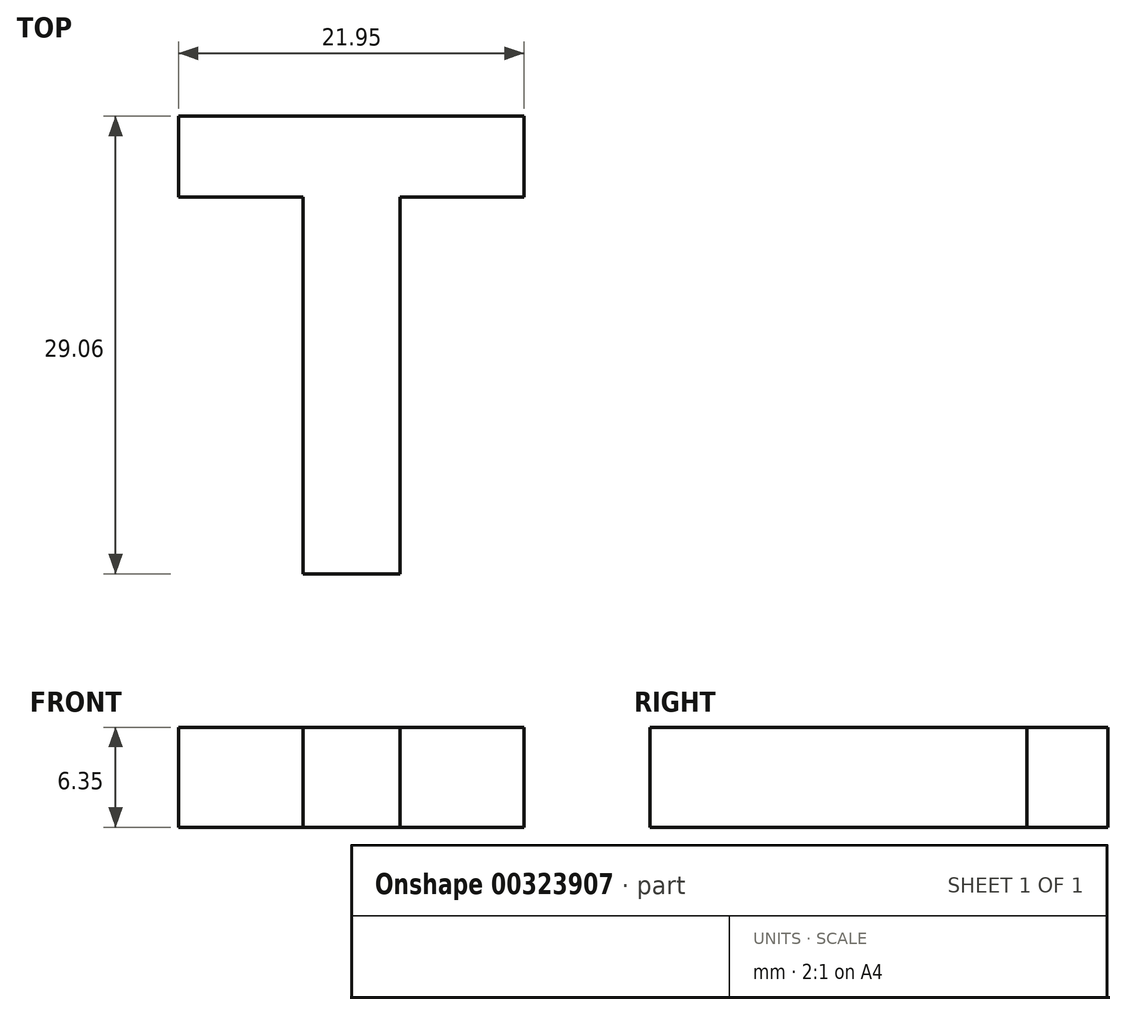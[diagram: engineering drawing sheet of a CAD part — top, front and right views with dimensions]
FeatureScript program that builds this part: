
annotation { "Feature Type Name" : "Feature", "Feature Type Description" : "" }
export const myFeature = defineFeature(function(context is Context, id is Id, definition is map)
    precondition{}
    {
        {
            var Q0;
            Q0=qCreatedBy(makeId("Top.planeOp"),FACE);
            var sketch = newSketch(context, id + "F0", { "sketchPlane" : qUnion([Q0])});
            skText(sketch, "E0", { "text": "T", "fontName": "OpenSans-Bold.ttf"});
            skLineSegment(sketch, "E1", {"start": v(12.7, 0) * mm, "end": v(19.25, 4.63) * mm, "construction": true});
            const initialGuessF0  = {"E0": [-0.0127, -0.01466, 1, 0, 0.02931]};
            skSetInitialGuess(sketch, initialGuessF0);
            skSolve(sketch);
        }
        {
            var Q0;
            Q0 = qSketchRegion(id + "F0", true);
            extrude(context, id + "F1", {"entities" : qUnion([Q0]), "depth" : 6.35 * mm});
        }
    });
